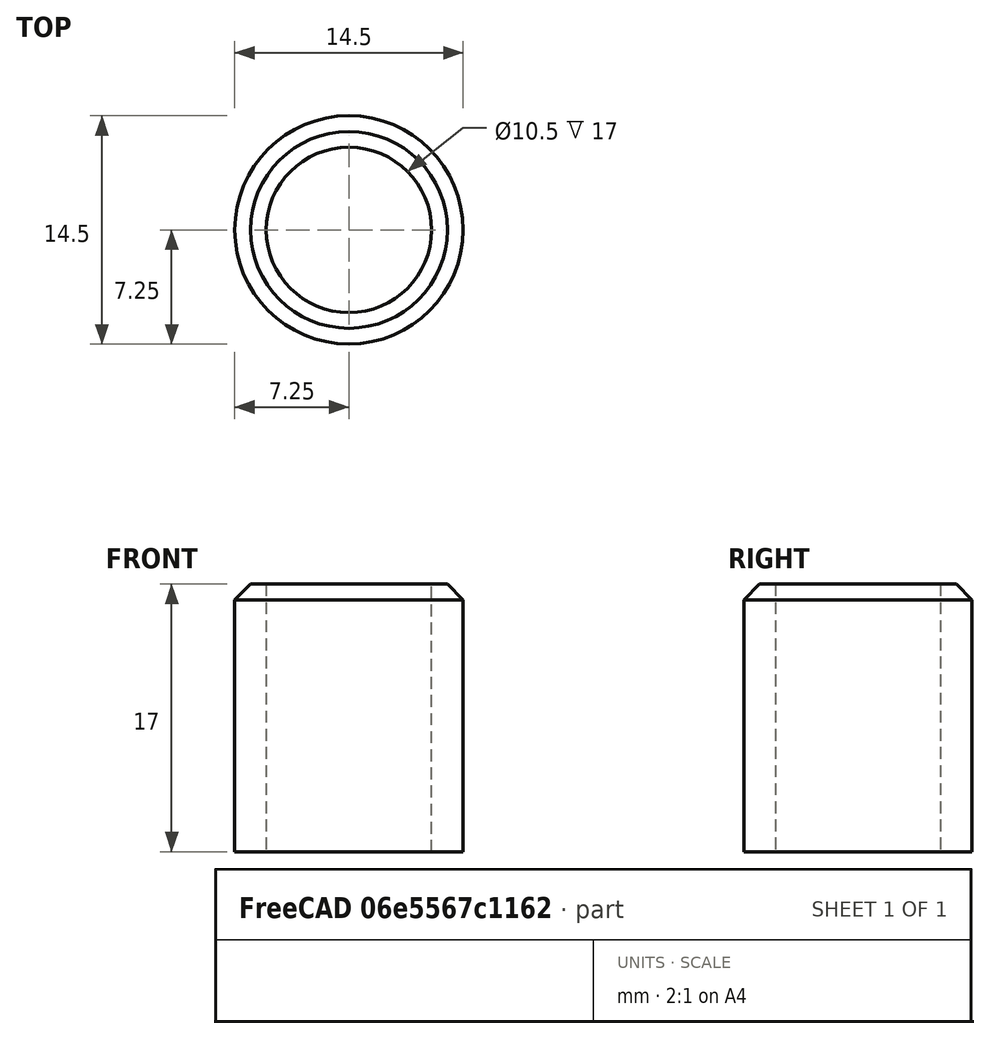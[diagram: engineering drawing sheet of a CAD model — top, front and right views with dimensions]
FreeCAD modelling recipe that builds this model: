
FCSTD DOCUMENT  (FreeCAD 2020.10.16R22739 +2665 (Git))
Label: tulejka-sruby
License: All rights reserved
LicenseURL: http://en.wikipedia.org/wiki/All_rights_reserved
objects: Sketcher::SketchObject×1, PartDesign::Pad×1, PartDesign::Chamfer×1, PartDesign::Body×1
note: 8 computed .brp shape members not serialized (recipe doc carries the construction recipe); baked Part::Feature solids carry a one-line shape summary decoded from their .brp

FEATURE [Sketcher::SketchObject] Sketch
  MapMode = 5
  Support = -> [XY_Plane]
  sketch-geometry (2):
    g0: Circle CenterX=0 CenterY=0 CenterZ=0 NormalX=0 NormalY=0 NormalZ=1 AngleXU=0 Radius=5.25
    g1: Circle CenterX=0 CenterY=0 CenterZ=0 NormalX=0 NormalY=0 NormalZ=1 AngleXU=0 Radius=7.25
  constraints (4):
    c: Coincident(g0,g-1)
    c: Coincident(g1,g0)
    c: Diameter(g0) = 10.5
    c: Diameter(g1) = 14.5
FEATURE [PartDesign::Pad] Pad
  ClaimChildren = false
  Direction = (1,1,1)
  Length = 17
  Length2 = 100
  NewSolid = false
  Profile = -> Sketch
  Suppress = false
  Type = 0
FEATURE [PartDesign::Chamfer] Chamfer
  Angle = 45
  Base = -> Pad [Edge3]
  BaseFeature = -> Pad
  ChamferType = 0
  FlipDirection = false
  NewSolid = false
  Size = 1
  Size2 = 1
  SupportTransform = true
  Suppress = false
FEATURE [PartDesign::Body] Body  label="tulejka-sruby"
  ExportMode = 0
  Group = -> [Sketch,Pad,Chamfer]
  Origin = -> Origin
  Tip = -> Chamfer
  _ExportChildren = -> [Pad,Chamfer]
  _GroupVersion = 1
